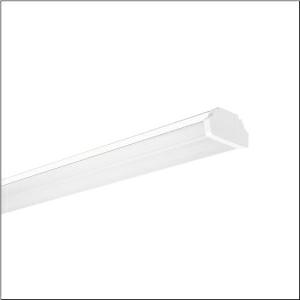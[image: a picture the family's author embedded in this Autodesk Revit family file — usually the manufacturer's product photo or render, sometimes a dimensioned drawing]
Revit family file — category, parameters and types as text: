
# Revit family: dus_r__31_mo_53bd812m1v4085_035f
name_source: partatom
category: Lighting Fixtures
units: mm (PartAtom-declared; Revit-internal decimal feet)

## family parameters
Cut with Voids When Loaded = No
Host = Face
Light Source = No
Part Type = Normal
Room Calculation Point = No
Round Connector Dimension = Use Diameter
Shared = No

## types (1)
- --- (1 x LED, 8950 lm, 59.6 W, 4000K)
    Apparent Load = 60 VA
    CIE Flux Codes = 47 80 95 92 100
    Color Rendering = 80
    Color Temperature = 4000K
    Default Elevation = 1800 mm
    Description = DUS® 31 MO, luminaire insert, of sheet steel, coil coated, white, length: 1.535mm, width: 81mm, height: 90mm, 5x system unit, system units: 307mm, LED rated luminous flux: 8.950lm, light colour: 840, control gear: ON/OFF Multilumen, control gear: ECG Multilumen, with plug, 3-pole, with phase selection, mains connection: 220..240V, AC, 50/60Hz, rated input power: 60W, through-wiring accessed according to module size, primary optical cover: cover, of PMMA, light emission: direct distribution, primary light characteristic: symmetric, protection rating (complete): IP20, protection rating (LED compartment): IP50, insulation class (complete): insulation class I (protective earthing), certification: CE, ENEC, VDE, UKCA, impact resistance: IK03, permissible ambient temperature for indoor applications: -35..+30°C, corresponds to IFS (International Featured Standards) requirements for safety and quality in the food industry, reducing of maximum allowable ambient temperature of 5°C with ceiling mounting, packaging unit: 1 piece
    Height = 95 mm
    Lamp = 1 x LED
    Lamp Light Flux = 8950 lm
    Lamp Power = 59.6 W
    Lamp count = 1
    Length = 1535 mm
    Luminous efficacy = 150 lm/W
    Manufacturer = Siteco
    ModVariant = No
    Model = 53BD812M1V4085
    Mounting Place = Ceiling
    Mounting Type = Pendant
    Number of Poles = 1
    OnlyDefault = Yes
    Power Factor = 1
    Product Name = DUS® 31 MO
    Product group = luminaire insert
    ProductGroupID = 901
    Protection Class = Protection class I
    Protection Degree = IP 20
    RLX_Detail_Level = 1
    RLX_Emergency_Light_Flux = 0 lm
    RLX_Emergency_Type = 0
    RLX_Emergency_Type_DB = No
    RlxData = <blob elided: 39745 chars, md5=859cd3fc>
    Socket = socket
    Standby Power = 0 W
    System Light Flux = 8950 lm
    System Power = 60 W
    Type Comments = factory setting: luminous flux: 100 % | (A | C | E) | 129 mA
    Type Image = l_1319596.jpg
    URL = http://relux.com
    VarID = @adj_173945
    Voltage = 0 V
    Weight = 0.00 kg
    Width = 81 mm

## geometry (parser evidence)
native form markers: Blend x4, Sweep x11
no freeform markers — native parametric forms only
